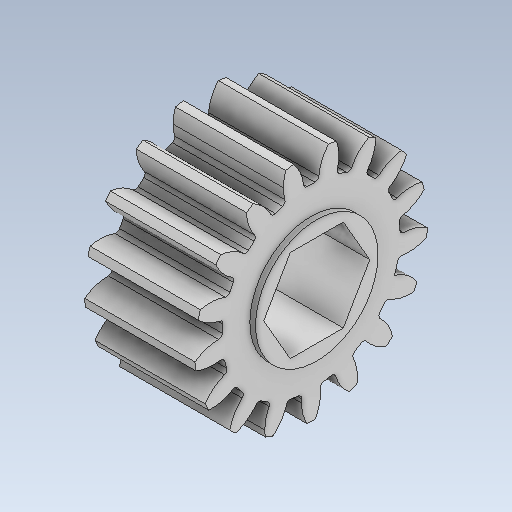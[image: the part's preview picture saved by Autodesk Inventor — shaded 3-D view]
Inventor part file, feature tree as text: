
AUTODESK INVENTOR PART (.ipt)
format: ipt  version: 2021 (Build 250183000, 183)  size: 299,008 bytes
history: native  units: in
note: dims shown in document units (in); Inventor stores cm internally (conversion verified against a paired STEP export)
features: fillet x1
ambient origin geometry x8: Origin, YZ Plane, XZ Plane, XY Plane, X Axis, Y Axis, Z Axis, Center Point
bodies: Solid1 (feature_tree)
feature tree (1):
  fillet  "Fillet1"  [1 undecoded]
note: 1 required parameter value undecoded (feature->parameter linkage not recoverable at this tier; creation-order binding heuristic only, values carry confidence <= 0.55)
